# Revit family: NBS_WallgateLtd_WlHngWshBsns_Thrii-SS
name_source: partatom
category: Plumbing Fixtures
revit_build: Autodesk Revit 2014 (Build: 20130709_2115(x64)
units: mm (PartAtom-declared; Revit-internal decimal feet)

## types (1)
- Thrii-SS
    ApetureHeight = 683 mm  [stored 2.24081 ft]
    ApetureWidth = 427 mm  [stored 1.40092 ft]
    AssetType = Fixed
    BIMObjectName = NBS_WallgateLtd_WallHungWashBasins_Thrii-SS
    BodyMaterial = Polyamide
    CloseOffRating = 0
    ColourOptions = MA - Thames, MAH - Frost, MAW - White, MC - Bluestone, MCA - Aubergine, MCB - Diamantina, MCC - Black, MCD - Orange, MCE - Pink, MO - Slate, MS - Hyco, MCJ - Light Grey, MCF - NHS Blue
    Description = Thrii solid surface automatic hand wash dryer
    DrainSize = 32 mm  [stored 0.104987 ft]
    DrainSizeOptions = 32 mm or 40 mm
    Durability = Compliant to Grade 5
    DurationUnit = year
    ElectricalDeviceNominalPower = 3100
    FaucetFunction = Mixed
    FaucetOperation = TimedSelfClosing
    FaucetType = Other
    Features = Hygienic and easily cleaned, highly vandal-resistant
    FixingMaterial = NBS_Concept
    FlowCoefficient = 1.5
    Form = Recessed hand wash dryer with soap, water, air hand washing and flush functionality
    HandDryingTime = 45 seconds (factory set)
    HasProtectiveEarth = Yes
    IP_Code = IPX4
    IfcExportAs = IfcSanitaryTerminalType
    IfcExportType = WASHHANDBASIN
    InsulationStandardClass = Class 1
    ManufacturerName = Wallgate Ltd
    ManufacturerURL = www.wallgate.com
    Material = High-grade solid surface material
    ModelNumber = Thrii-SS
    NBSCertification = www.nationalbimlibrary.com/cert/oesvf2oc
    NBSDescription = Wall hung wash basins
    NBSReference = 45-35-70/369
    Name = WallHungWashBasins_Thrii-SS_WallgateLtd
    NoiseLevelAtOneMetreMaximum = 88 db(A)
    NominalCurrent = 13
    NominalDepth = 310 mm
    NominalFrequencyRange = 50.0 , 60.0
    NominalHeight = 870 mm
    NominalLength = 0 mm  [stored 0 ft]
    NominalVoltage = 220.0 , 240.0
    NominalWidth = 450 mm
    NumberOfPoles = 2
    Operation = Automatic infra-red sensor
    Outlets = Single outlet
    PhaseAngle = 0.00°
    PhaseReference = Single Phase
    ProductInformation = www.wallgate.com/products/hand-wash-dryers/thrii-range
    Size = 15.0
    SoapCapacityOptions = 2.5 or 5 L, foam or liquid
    SoapCompatibility = Wallgate Walcare 208
    TestPressure = 10.0
    Uniclass2 = 45-31-79/494
    UsageCurrent = 13
    ValveMechanism = Unset
    ValveOperation = Other
    ValvePattern = Unset
    Version = 1
    WarrantyDurationParts = 1
    WarrantyDurationUnit = year
    WashBasinMaterial = NBS_Concept
    WashHandBasinMounting = Other
    WashHandBasinType = HandRinse
    WaterDispensingTime = 10 seconds (factory set)
    WaterSupplyFittingMaterial = NBS_Concept
    WaterSupplyOverflowAndWasteHolesOverflow = None
    WaterSupplyOverflowAndWasteHolesWaste = Bottom waste outlet
    WaterSupplyTemperatureMaximum = 30°C to 45°C
    Weight = 29.4 kg
    WorkingPressure = 0

note: [stored X ft] marks values corroborated as IEEE doubles in the binary element streams (Revit-internal decimal feet)

## geometry (parser evidence)
native form markers: Sweep x2
no freeform markers — native parametric forms only
